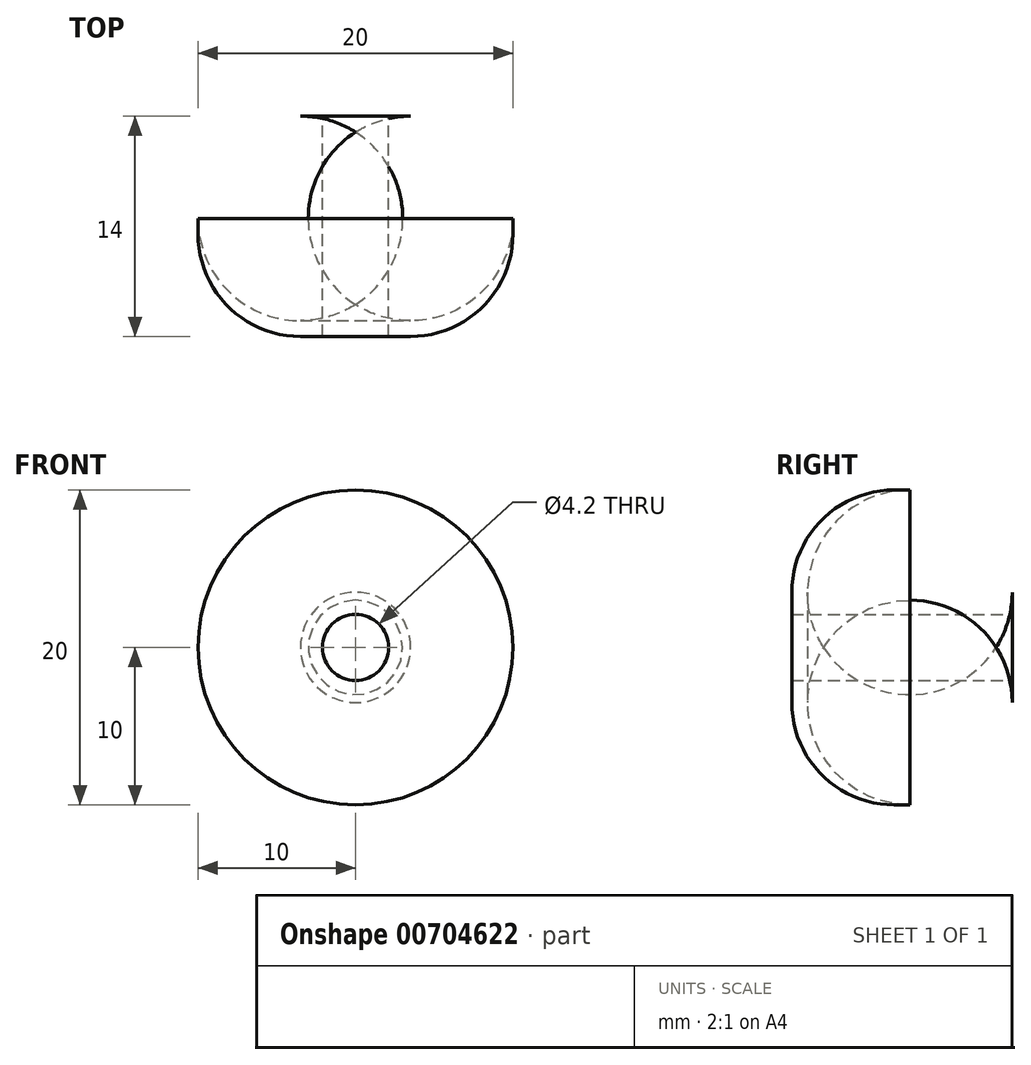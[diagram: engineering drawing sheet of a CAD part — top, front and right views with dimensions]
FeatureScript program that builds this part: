
annotation { "Feature Type Name" : "Feature", "Feature Type Description" : "" }
export const myFeature = defineFeature(function(context is Context, id is Id, definition is map)
    precondition{}
    {
        {
            var Q0;
            Q0=qCreatedBy(makeId("Front.planeOp"),FACE);
            var sketch = newSketch(context, id + "F0", { "sketchPlane" : qUnion([Q0])});
            skCircle(sketch, "E0", {"center": v(0, 0) * mm, "radius": 2.1 * mm});
            skCircle(sketch, "E1", {"center": v(0, 0) * mm, "radius": 10 * mm});
            skSolve(sketch);
        }
        {
            var Q0;
            Q0=sQuery(id+"F0.wireOp",EDGE,"E0");
            extrude(context, id + "F1", {"bodyType" : ToolBodyType.SURFACE, "surfaceEntities" : qUnion([Q0]), "depth" : 7.3 * mm, "offsetDistance" : 25.4 * mm, "hasSecondDirection" : true, "secondDirectionOppositeDirection" : true, "secondDirectionDepth" : 7.3 * mm});
        }
        {
            var Q0;
            Q0=makeQuery(id+"F0.imprint","IMPRINT",FACE,{"disambiguationData":[TD([[makeQuery(id+"F0.imprint","IMPRINT",EDGE,{"derivedFrom":sQuery(id+"F0.wireOp",EDGE,"E0")}),-1.0]])]});
            extrude(context, id + "F2", {"entities" : qUnion([Q0]), "depth" : 7 * mm, "offsetDistance" : 25.4 * mm, "hasSecondDirection" : true, "secondDirectionOppositeDirection" : true, "secondDirectionDepth" : 7 * mm});
        }
        {
            var Q0;
            Q0=makeQuery(id+"F2.opExtrude","CAP_EDGE",EDGE,{"disambiguationData":[OSD([sQuery(id+"F0.wireOp",EDGE,"E1")])],"isStart":false});
            var Q1;
            Q1=makeQuery(id+"F2.opExtrude","CAP_EDGE",EDGE,{"disambiguationData":[OSD([sQuery(id+"F0.wireOp",EDGE,"E1")])],"isStart":true});
            fillet(context, id + "F3", {"entities" : qUnion([Q0, Q1]), "radius" : 6.5 * mm, "tangentPropagation" : true, "allowEdgeOverflow" : false});
        }
    });
